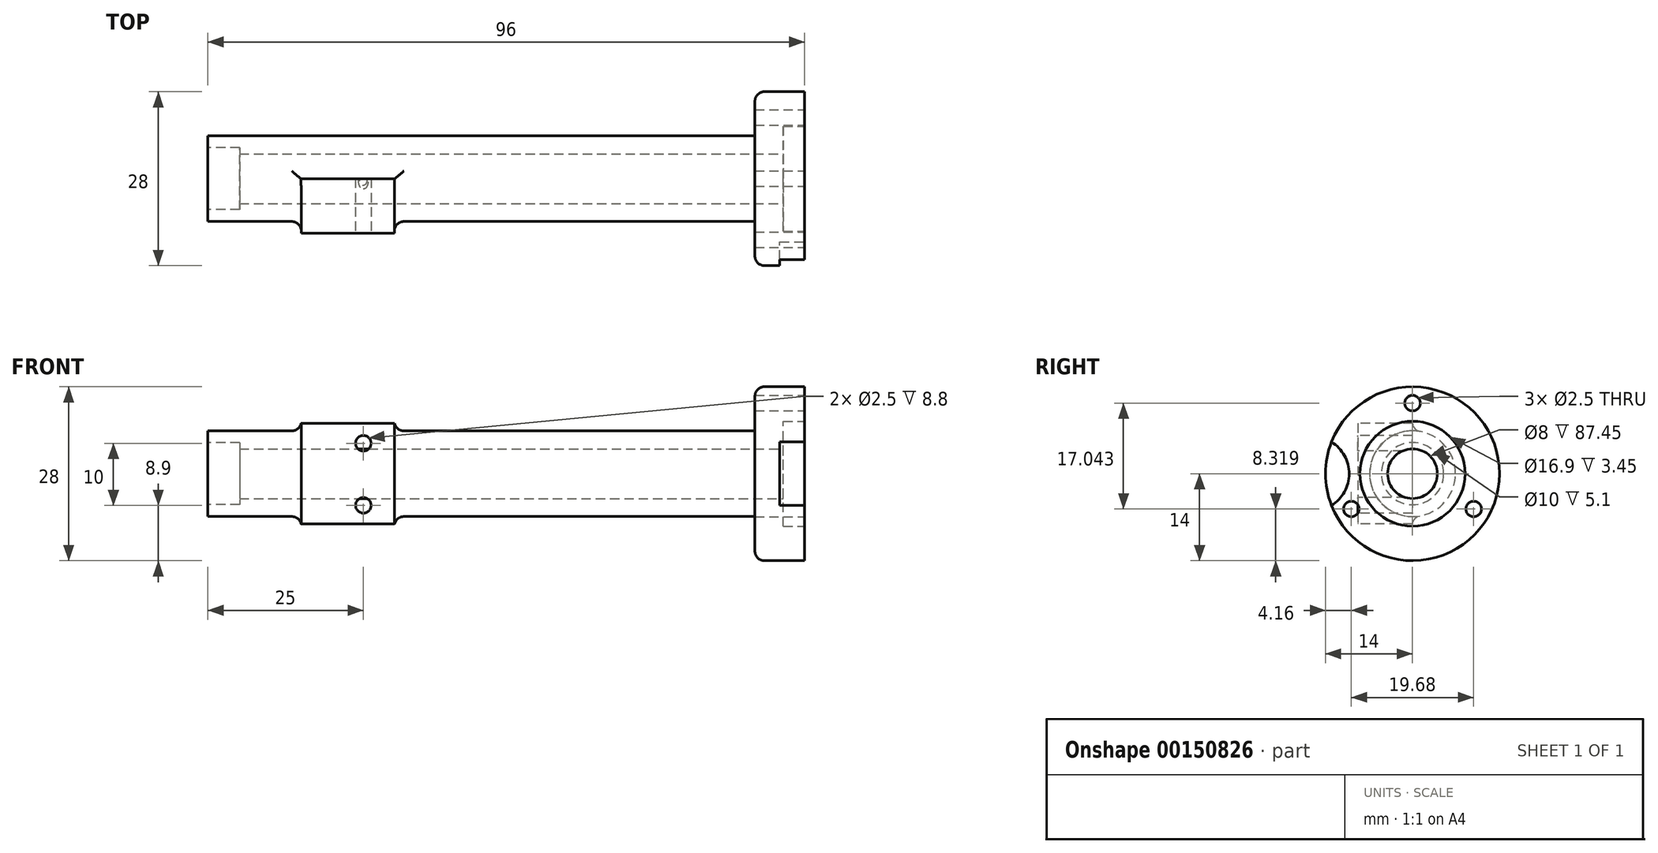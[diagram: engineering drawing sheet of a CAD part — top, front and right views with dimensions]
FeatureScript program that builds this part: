
annotation { "Feature Type Name" : "Feature", "Feature Type Description" : "" }
export const myFeature = defineFeature(function(context is Context, id is Id, definition is map)
    precondition{}
    {
        {
            var Q0;
            Q0=qCreatedBy(makeId("Right.planeOp"),FACE);
            var sketch = newSketch(context, id + "F0", { "sketchPlane" : qUnion([Q0])});
            skCircle(sketch, "E0", {"center": v(0, 0) * mm, "radius": 14 * mm});
            skSolve(sketch);
        }
        {
            var Q0;
            Q0=makeQuery(id+"F0.imprint","IMPRINT",FACE,{"disambiguationData":[TD([[makeQuery(id+"F0.imprint","IMPRINT",EDGE,{"derivedFrom":sQuery(id+"F0.wireOp",EDGE,"E0")}),1.0]])]});
            extrude(context, id + "F1", {"entities" : qUnion([Q0]), "depth" : 8 * mm});
        }
        {
            var Q0;
            Q0=makeQuery(id+"F1.opExtrude","CAP_FACE",FACE,{"disambiguationData":[OSD([sQuery(id+"F0.wireOp",EDGE,"E0")])],"isStart":false});
            var sketch = newSketch(context, id + "F2", { "sketchPlane" : qUnion([Q0])});
            skCircle(sketch, "E1", {"center": v(0, 0) * mm, "radius": 8.45 * mm});
            skSolve(sketch);
        }
        {
            var Q0;
            Q0=qSketchRegion(id+"F2",true);
            extrude(context, id + "F3", {"entities" : qUnion([Q0]), "operationType" : NewBodyOperationType.REMOVE, "oppositeDirection" : true, "depth" : 3.45 * mm});
        }
        {
            var Q0;
            Q0=makeQuery(id+"F1.opExtrude","CAP_FACE",FACE,{"disambiguationData":[OSD([sQuery(id+"F0.wireOp",EDGE,"E0")])],"isStart":false});
            var sketch = newSketch(context, id + "F4", { "sketchPlane" : qUnion([Q0])});
            skCircle(sketch, "E2", {"center": v(0, 0) * mm, "radius": 11.36 * mm, "construction": true});
            skCircle(sketch, "E3", {"center": v(0, 11.36) * mm, "radius": 1.25 * mm});
            skCircle(sketch, "E4.1.0", {"center": v(-9.84, -5.68) * mm, "radius": 1.25 * mm});
            skCircle(sketch, "E4.2.0", {"center": v(9.84, -5.68) * mm, "radius": 1.25 * mm});
            skSolve(sketch);
        }
        {
            var Q0;
            Q0=makeQuery(id+"F4.imprint","IMPRINT",FACE,{"disambiguationData":[TD([[makeQuery(id+"F4.imprint","IMPRINT",EDGE,{"derivedFrom":sQuery(id+"F4.wireOp",EDGE,"E3")}),1.0]])]});
            var Q1;
            Q1=makeQuery(id+"F4.imprint","IMPRINT",FACE,{"disambiguationData":[TD([[makeQuery(id+"F4.imprint","IMPRINT",EDGE,{"derivedFrom":sQuery(id+"F4.wireOp",EDGE,"E4.1.0")}),1.0]])]});
            var Q2;
            Q2=makeQuery(id+"F4.imprint","IMPRINT",FACE,{"disambiguationData":[TD([[makeQuery(id+"F4.imprint","IMPRINT",EDGE,{"derivedFrom":sQuery(id+"F4.wireOp",EDGE,"E4.2.0")}),1.0]])]});
            extrude(context, id + "F5", {"entities" : qUnion([Q0, Q1, Q2]), "operationType" : NewBodyOperationType.REMOVE, "endBound" : BoundingType.THROUGH_ALL, "oppositeDirection" : true, "depth" : 25 * mm});
        }
        {
            var Q0;
            Q0=makeQuery(id+"F1.opExtrude","CAP_FACE",FACE,{"disambiguationData":[OSD([sQuery(id+"F0.wireOp",EDGE,"E0")])],"isStart":true});
            var sketch = newSketch(context, id + "F6", { "sketchPlane" : qUnion([Q0])});
            skCircle(sketch, "E5", {"center": v(0, 0) * mm, "radius": 6.9 * mm});
            skSolve(sketch);
        }
        {
            var Q0;
            Q0=makeQuery(id+"F6.imprint","IMPRINT",FACE,{"disambiguationData":[TD([[makeQuery(id+"F6.imprint","IMPRINT",EDGE,{"derivedFrom":sQuery(id+"F6.wireOp",EDGE,"E5")}),1.0]])]});
            extrude(context, id + "F7", {"entities" : qUnion([Q0]), "operationType" : NewBodyOperationType.ADD, "depth" : 88 * mm});
        }
        {
            var Q0;
            Q0=qCreatedBy(makeId("Top.planeOp"),FACE);
            var sketch = newSketch(context, id + "F8", { "sketchPlane" : qUnion([Q0])});
            skLineSegment(sketch, "E6.bottom", {"start": v(-73, 0) * mm, "end": v(-58, 0) * mm});
            skLineSegment(sketch, "E6.top", {"start": v(-73, -8.8) * mm, "end": v(-58, -8.8) * mm});
            skLineSegment(sketch, "E6.left", {"start": v(-73, 0) * mm, "end": v(-73, -8.8) * mm});
            skLineSegment(sketch, "E6.right", {"start": v(-58, 0) * mm, "end": v(-58, -8.8) * mm});
            skSolve(sketch);
        }
        {
            var Q0;
            Q0=makeQuery(id+"F8.imprint","IMPRINT",FACE,{"disambiguationData":[TD([[makeQuery(id+"F8.imprint","IMPRINT",EDGE,{"derivedFrom":sQuery(id+"F8.wireOp",EDGE,"E6.bottom")}),-1.0]])]});
            extrude(context, id + "F9", {"entities" : qUnion([Q0]), "operationType" : NewBodyOperationType.ADD, "endBound" : BoundingType.SYMMETRIC, "depth" : 16.2 * mm});
        }
        {
            var Q0;
            Q0=makeQuery(id+"F1.opExtrude","CAP_FACE",FACE,{"disambiguationData":[OSD([sQuery(id+"F0.wireOp",EDGE,"E0")])],"isStart":false});
            var sketch = newSketch(context, id + "F10", { "sketchPlane" : qUnion([Q0])});
            skCircle(sketch, "E7", {"center": v(0, 0) * mm, "radius": 4 * mm});
            skSolve(sketch);
        }
        {
            var Q0;
            Q0=makeQuery(id+"F10.imprint","IMPRINT",FACE,{"disambiguationData":[TD([[makeQuery(id+"F10.imprint","IMPRINT",EDGE,{"derivedFrom":sQuery(id+"F10.wireOp",EDGE,"E7")}),1.0]])]});
            extrude(context, id + "F11", {"entities" : qUnion([Q0]), "operationType" : NewBodyOperationType.REMOVE, "endBound" : BoundingType.THROUGH_ALL, "oppositeDirection" : true, "depth" : 25 * mm});
        }
        {
            var Q0;
            Q0=makeQuery(id+"F7.opExtrude","CAP_FACE",FACE,{"disambiguationData":[OSD([sQuery(id+"F6.wireOp",EDGE,"E5")])],"isStart":false});
            var sketch = newSketch(context, id + "F12", { "sketchPlane" : qUnion([Q0])});
            skCircle(sketch, "E8", {"center": v(0, 0) * mm, "radius": 5 * mm});
            skSolve(sketch);
        }
        {
            var Q0;
            Q0=makeQuery(id+"F12.imprint","IMPRINT",FACE,{"disambiguationData":[TD([[makeQuery(id+"F12.imprint","IMPRINT",EDGE,{"derivedFrom":sQuery(id+"F12.wireOp",EDGE,"E8")}),1.0]])]});
            extrude(context, id + "F13", {"entities" : qUnion([Q0]), "operationType" : NewBodyOperationType.REMOVE, "oppositeDirection" : true, "depth" : 5.1 * mm});
        }
        {
            var Q0;
            Q0=makeQuery(id+"F9.opExtrude","SWEPT_FACE",FACE,{"disambiguationData":[OSD([sQuery(id+"F8.wireOp",EDGE,"E6.top")])]});
            var sketch = newSketch(context, id + "F14", { "sketchPlane" : qUnion([Q0])});
            skCircle(sketch, "E9", {"center": v(-63, -5.1) * mm, "radius": 1.25 * mm});
            skLineSegment(sketch, "E10", {"start": v(-63, -16.17) * mm, "end": v(-63, 16.97) * mm, "construction": true});
            skCircle(sketch, "E11", {"center": v(-63, 4.9) * mm, "radius": 1.25 * mm});
            skSolve(sketch);
        }
        {
            var Q0;
            Q0=makeQuery(id+"F14.imprint","IMPRINT",FACE,{"disambiguationData":[TD([[makeQuery(id+"F14.imprint","IMPRINT",EDGE,{"derivedFrom":sQuery(id+"F14.wireOp",EDGE,"E11")}),1.0]])]});
            var Q1;
            Q1=makeQuery(id+"F14.imprint","IMPRINT",FACE,{"disambiguationData":[TD([[makeQuery(id+"F14.imprint","IMPRINT",EDGE,{"derivedFrom":sQuery(id+"F14.wireOp",EDGE,"E9")}),1.0]])]});
            extrude(context, id + "F15", {"entities" : qUnion([Q0, Q1]), "operationType" : NewBodyOperationType.REMOVE, "oppositeDirection" : true, "depth" : 8.8 * mm});
        }
        {
            var Q0;
            Q0=makeQuery(id+"F1.opExtrude","CAP_FACE",FACE,{"disambiguationData":[OSD([sQuery(id+"F0.wireOp",EDGE,"E0")])],"isStart":false});
            var sketch = newSketch(context, id + "F16", { "sketchPlane" : qUnion([Q0])});
            skCircle(sketch, "E12", {"center": v(-16.2, 0) * mm, "radius": 6 * mm});
            skSolve(sketch);
        }
        {
            var Q0;
            Q0=qSketchRegion(id+"F16",true);
            extrude(context, id + "F17", {"entities" : qUnion([Q0]), "operationType" : NewBodyOperationType.REMOVE, "oppositeDirection" : true, "depth" : 4 * mm});
        }
        {
            var Q0;
            Q0=makeQuery(id+"F7.opExtrude","CAP_EDGE",EDGE,{"disambiguationData":[OSD([sQuery(id+"F6.wireOp",EDGE,"E5")])],"isStart":true});
            var Q1;
            Q1=makeQuery(id+"F9.boolean.opBoolean","INTERSECT",EDGE,{"derivedFrom":[makeQuery(id+"F7.opExtrude","SWEPT_FACE",FACE,{"disambiguationData":[OSD([sQuery(id+"F6.wireOp",EDGE,"E5")])]}),makeQuery(id+"F9.opExtrude","SWEPT_FACE",FACE,{"disambiguationData":[OSD([sQuery(id+"F8.wireOp",EDGE,"E6.left")])]})]});
            var Q2;
            Q2=makeQuery(id+"F9.boolean.opBoolean","INTERSECT",EDGE,{"derivedFrom":[makeQuery(id+"F7.opExtrude","SWEPT_FACE",FACE,{"disambiguationData":[OSD([sQuery(id+"F6.wireOp",EDGE,"E5")])]}),makeQuery(id+"F9.opExtrude","SWEPT_FACE",FACE,{"disambiguationData":[OSD([sQuery(id+"F8.wireOp",EDGE,"E6.right")])]})]});
            var Q3;
            Q3=makeQuery(id+"F9.boolean.opBoolean","INTERSECT",EDGE,{"disambiguationData":[OD(1.0)],"derivedFrom":[makeQuery(id+"F7.opExtrude","SWEPT_FACE",FACE,{"disambiguationData":[OSD([sQuery(id+"F6.wireOp",EDGE,"E5")])]}),makeQuery(id+"F9.opExtrude","SWEPT_FACE",FACE,{"disambiguationData":[OSD([sQuery(id+"F8.wireOp",EDGE,"E6.bottom")])]})]});
            var Q4;
            Q4=makeQuery(id+"F9.boolean.opBoolean","INTERSECT",EDGE,{"disambiguationData":[OD(0.0)],"derivedFrom":[makeQuery(id+"F7.opExtrude","SWEPT_FACE",FACE,{"disambiguationData":[OSD([sQuery(id+"F6.wireOp",EDGE,"E5")])]}),makeQuery(id+"F9.opExtrude","SWEPT_FACE",FACE,{"disambiguationData":[OSD([sQuery(id+"F8.wireOp",EDGE,"E6.bottom")])]})]});
            fillet(context, id + "F18", {"entities" : qUnion([Q0, Q1, Q2, Q3, Q4]), "radius" : 1.5 * mm, "tangentPropagation" : true, "allowEdgeOverflow" : false});
        }
        {
            var Q0;
            Q0=makeQuery(id+"F1.opExtrude","CAP_EDGE",EDGE,{"disambiguationData":[OSD([sQuery(id+"F0.wireOp",EDGE,"E0")])],"isStart":true});
            fillet(context, id + "F19", {"entities" : qUnion([Q0]), "radius" : 1.5 * mm, "tangentPropagation" : true, "allowEdgeOverflow" : false});
        }
    });
